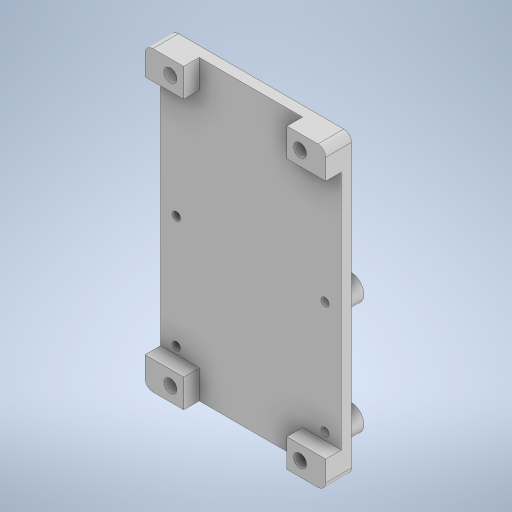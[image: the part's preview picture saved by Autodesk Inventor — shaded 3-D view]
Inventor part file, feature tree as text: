
AUTODESK INVENTOR PART (.ipt)
format: ipt  version: 2023 (Build 270158000, 158)  size: 340,992 bytes
history: native  units: mm
features: sketch x5, extrude x5, projected_geometry x3, other x1, hole x1
ambient origin geometry x8: Origin, YZ Plane, XZ Plane, XY Plane, X Axis, Y Axis, Z Axis, Center Point
bodies: Body1 (feature_tree)
feature tree (15):
  other  "솔리드1"
  sketch  "스케치1"
  extrude  "돌출1"  Depth=35.0mm
  extrude  "돌출2"  Depth=57.6mm
  sketch  "스케치3"
  extrude  "돌출3"  Depth=25.1mm
  extrude  "돌출4"  Depth=52.1mm
  extrude  "돌출5"  Depth=2.5mm
  hole  "구멍2"  [1 undecoded]
  sketch  "스케치4"
  sketch  "스케치5"
  sketch  "스케치6"
  projected_geometry  "투영된 루프1"
  projected_geometry  "투영된 루프2"
  projected_geometry  "투영된 루프3"
note: 1 required parameter value undecoded (feature->parameter linkage not recoverable at this tier; creation-order binding heuristic only, values carry confidence <= 0.55)
